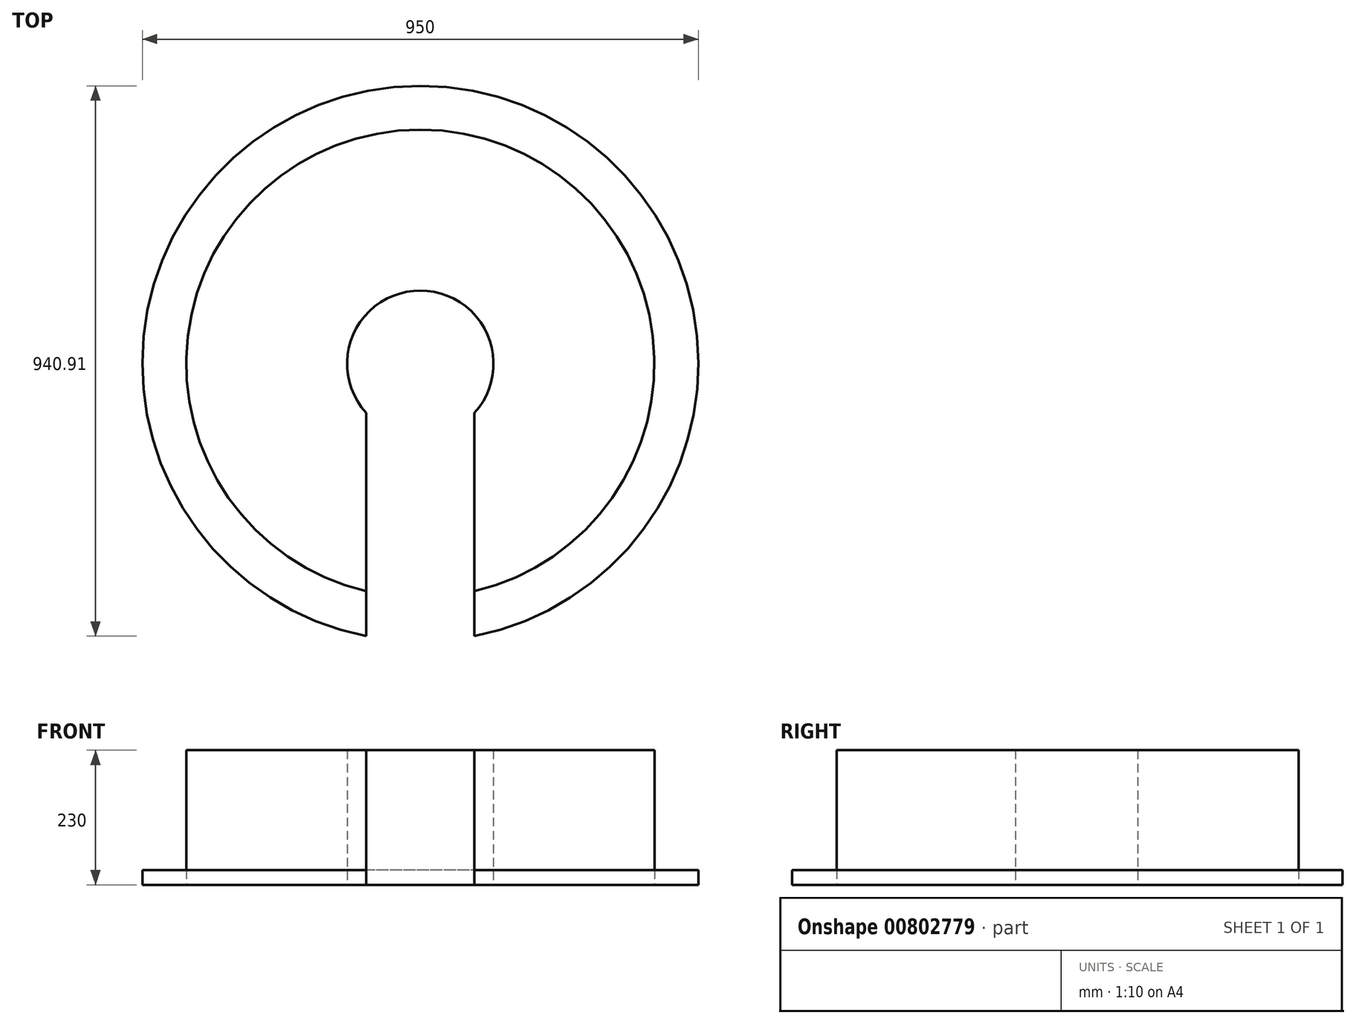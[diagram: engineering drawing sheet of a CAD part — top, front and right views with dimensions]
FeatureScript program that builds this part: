
annotation { "Feature Type Name" : "Feature", "Feature Type Description" : "" }
export const myFeature = defineFeature(function(context is Context, id is Id, definition is map)
    precondition{}
    {
        {
            var Q0;
            Q0=qCreatedBy(makeId("Top.planeOp"),FACE);
            var sketch = newSketch(context, id + "F0", { "sketchPlane" : qUnion([Q0])});
            skArc(sketch, "E0", {"start": v(92.5, -389.16) * mm, "mid": v(0, 400) * mm, "end": v(-92.5, -389.16) * mm});
            skArc(sketch, "E1", {"start": v(92.5, -84.08) * mm, "mid": v(0, 125) * mm, "end": v(-92.5, -84.08) * mm});
            skLineSegment(sketch, "E2", {"start": v(-92.5, -84.08) * mm, "end": v(-92.5, -465.9) * mm});
            skLineSegment(sketch, "E3", {"start": v(0, 0) * mm, "end": v(0, -80.35) * mm, "construction": true});
            skLineSegment(sketch, "E4.MirrorCS", {"start": v(92.5, -84.08) * mm, "end": v(92.5, -465.9) * mm});
            skPoint(sketch, "E5.orphan", {"position": v(-92.5, -12.09) * mm});
            skPoint(sketch, "E6.orphan", {"position": v(92.5, -12.09) * mm});
            skPoint(sketch, "E7.orphan", {"position": v(-92.5, -439.56) * mm});
            skPoint(sketch, "E8.orphan", {"position": v(92.5, -439.56) * mm});
            skCircle(sketch, "E9", {"center": v(0, 0) * mm, "radius": 475 * mm});
            skSolve(sketch);
        }
        {
            var Q0;
            {var subQ0=sQuery(id+"F0.wireOp",EDGE,"E0");Q0=makeQuery(id+"F0.imprint","IMPRINT",FACE,{"disambiguationData":[TD([[makeQuery(id+"F0.imprint","IMPRINT",EDGE,{"derivedFrom":subQ0}),1.0]])]});}
            extrude(context, id + "F1", {"entities" : qUnion([Q0]), "depth" : 230 * mm});
        }
        {
            var Q0;
            {var subQ0=sQuery(id+"F0.wireOp",EDGE,"E0");Q0=makeQuery(id+"F0.imprint","IMPRINT",FACE,{"disambiguationData":[TD([[makeQuery(id+"F0.imprint","IMPRINT",EDGE,{"derivedFrom":subQ0}),-1.0]])]});}
            extrude(context, id + "F2", {"entities" : qUnion([Q0]), "depth" : 25 * mm});
        }
    });
